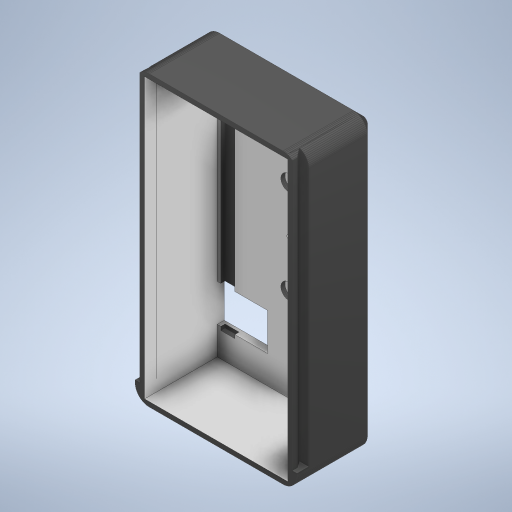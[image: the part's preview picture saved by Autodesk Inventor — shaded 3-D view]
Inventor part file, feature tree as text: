
AUTODESK INVENTOR PART (.ipt)
format: ipt  version: 2024.3 (Build 283343000, 343)  size: 1,375,232 bytes
history: native  units: mm
features: other x4, extrude x3, sketch x3
ambient origin geometry x8: Origin, YZ Plane, XZ Plane, XY Plane, X Axis, Y Axis, Z Axis, Center Point
bodies: Body1 (feature_tree)
feature tree (10):
  other  "ESP32_DEVKIT_V1_Carcasa.ipt"
  extrude  "Extrusión1"  Depth=20.0mm
  extrude  "Extrusión5"  Depth=29.0mm
  extrude  "Extrusión6"  Depth=2.0mm
  other  "Sólido1::ESP32_DEVKIT_V1_Carcasa.ipt"
  other  "OperaciónIdentificador1"
  sketch  "Boceto1"  dims[d0=20.0mm d1=1.85mm]
  sketch  "Boceto5"  dims[d2=49.0mm d3=29.0mm]
  sketch  "Boceto6"  dims[d4=10.0mm d5=0.0mm d21=2.0mm d22=2.0mm d23=2.0mm d24=2.0mm d25=31.0mm d26=0.0mm d30=10.0mm d31=21.4mm d32=15.9mm d33=10.0mm d34=0.0mm d35=0.0mm]
  other  "Sólido1"
